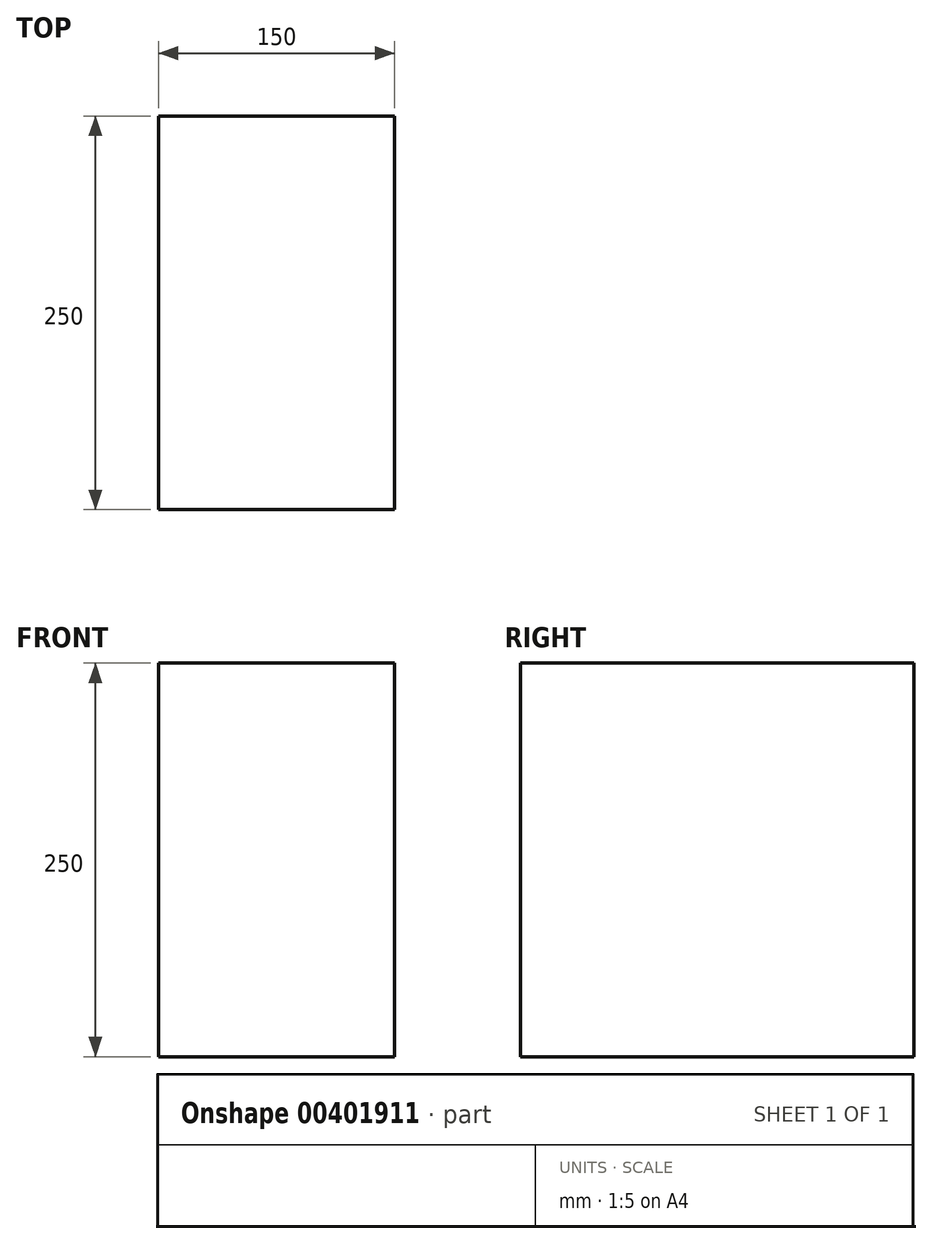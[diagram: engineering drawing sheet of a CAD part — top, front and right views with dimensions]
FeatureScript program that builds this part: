
annotation { "Feature Type Name" : "Feature", "Feature Type Description" : "" }
export const myFeature = defineFeature(function(context is Context, id is Id, definition is map)
    precondition{}
    {
        {
            var Q0;
            Q0=qCreatedBy(makeId("Front.planeOp"),FACE);
            var sketch = newSketch(context, id + "F0", { "sketchPlane" : qUnion([Q0])});
            skLineSegment(sketch, "E0.bottom", {"start": v(-75.9, 181.63) * mm, "end": v(74.1, 181.63) * mm});
            skLineSegment(sketch, "E0.top", {"start": v(-75.9, -68.37) * mm, "end": v(74.1, -68.37) * mm});
            skLineSegment(sketch, "E0.left", {"start": v(-75.9, 181.63) * mm, "end": v(-75.9, -68.37) * mm});
            skLineSegment(sketch, "E0.right", {"start": v(74.1, 181.63) * mm, "end": v(74.1, -68.37) * mm});
            skSolve(sketch);
        }
        {
            var Q0;
            Q0 = qSketchRegion(id + "F0", true);
            extrude(context, id + "F1", {"entities" : qUnion([Q0]), "depth" : 250 * mm});
        }
    });
